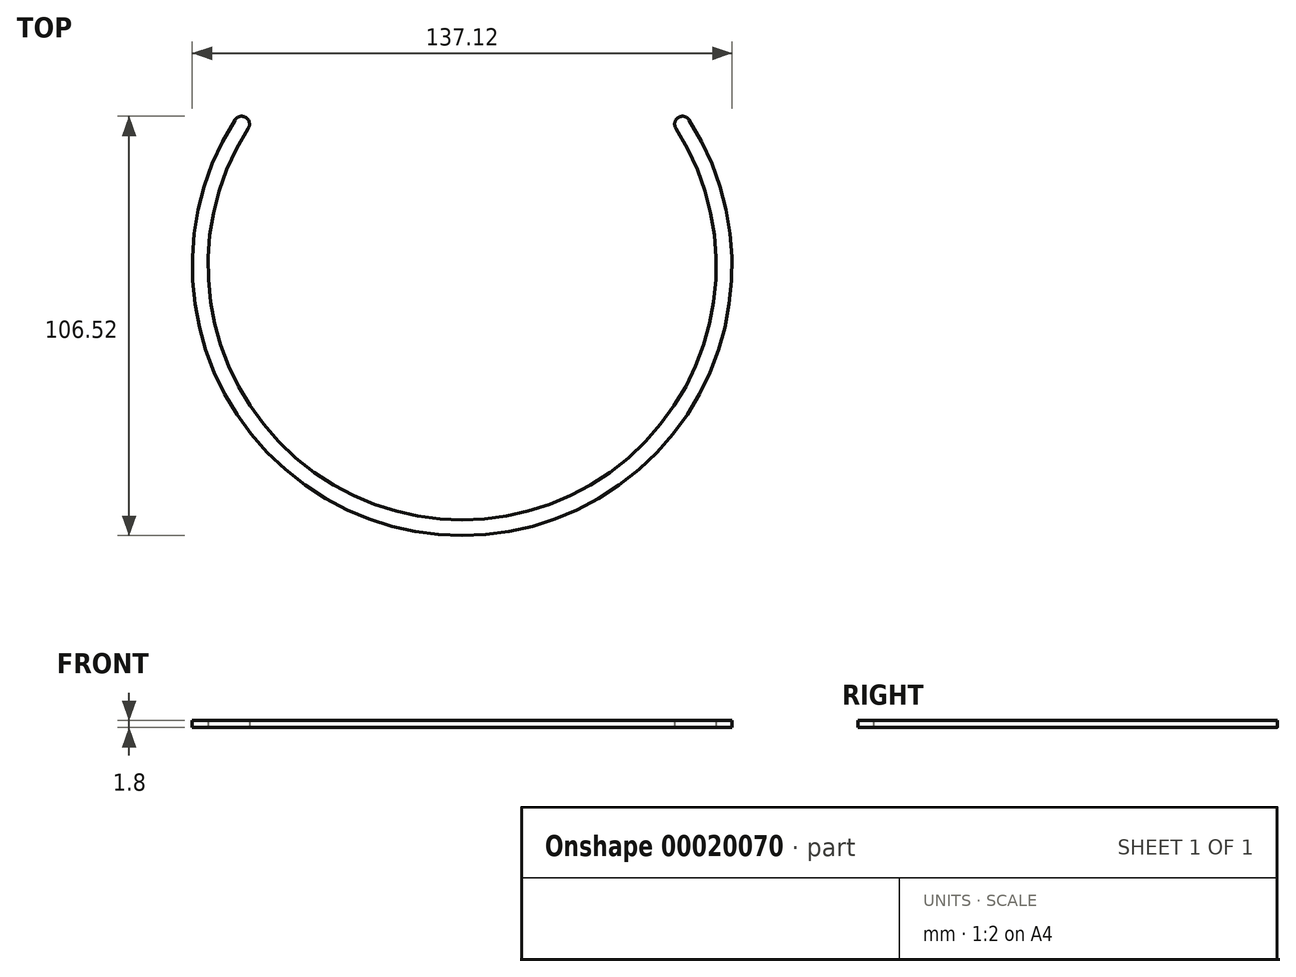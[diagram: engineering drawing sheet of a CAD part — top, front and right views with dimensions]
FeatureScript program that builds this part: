
annotation { "Feature Type Name" : "Feature", "Feature Type Description" : "" }
export const myFeature = defineFeature(function(context is Context, id is Id, definition is map)
    precondition{}
    {
        {
            var Q0;
            Q0=qCreatedBy(makeId("Top.planeOp"),FACE);
            var sketch = newSketch(context, id + "F0", { "sketchPlane" : qUnion([Q0])});
            skArc(sketch, "E0", {"start": v(-53.25, 36.5) * mm, "mid": v(0, -64.56) * mm, "end": v(53.25, 36.5) * mm});
            skArc(sketch, "E1", {"start": v(-56.55, 38.76) * mm, "mid": v(0, -68.56) * mm, "end": v(56.55, 38.76) * mm});
            skLineSegment(sketch, "E2", {"start": v(-53.25, 36.5) * mm, "end": v(-56.55, 38.76) * mm});
            skLineSegment(sketch, "E3", {"start": v(56.55, 38.76) * mm, "end": v(53.25, 36.5) * mm});
            skLineSegment(sketch, "E4", {"start": v(-53.25, 36.5) * mm, "end": v(-53.25, 0) * mm, "construction": true});
            skLineSegment(sketch, "E5", {"start": v(53.25, 36.5) * mm, "end": v(53.25, 0) * mm, "construction": true});
            skSolve(sketch);
        }
        {
            var Q0;
            Q0=makeQuery(id+"F0.imprint","IMPRINT",FACE,{"disambiguationData":[TD([[makeQuery(id+"F0.imprint","IMPRINT",EDGE,{"derivedFrom":sQuery(id+"F0.wireOp",EDGE,"E0")}),-1.0]])]});
            extrude(context, id + "F1", {"entities" : qUnion([Q0]), "depth" : 1.8 * mm});
        }
        {
            var Q0;
            Q0=makeQuery(id+"F1.opExtrude","SWEPT_EDGE",EDGE,{"disambiguationData":[OSD([sQuery(id+"F0.wireOp",EDGE,"E1"),sQuery(id+"F0.wireOp",EDGE,"E2")])]});
            var Q1;
            Q1=makeQuery(id+"F1.opExtrude","SWEPT_EDGE",EDGE,{"disambiguationData":[OSD([sQuery(id+"F0.wireOp",EDGE,"E0"),sQuery(id+"F0.wireOp",EDGE,"E2")])]});
            var Q2;
            Q2=makeQuery(id+"F1.opExtrude","SWEPT_EDGE",EDGE,{"disambiguationData":[OSD([sQuery(id+"F0.wireOp",EDGE,"E0"),sQuery(id+"F0.wireOp",EDGE,"E3")])]});
            var Q3;
            Q3=makeQuery(id+"F1.opExtrude","SWEPT_EDGE",EDGE,{"disambiguationData":[OSD([sQuery(id+"F0.wireOp",EDGE,"E1"),sQuery(id+"F0.wireOp",EDGE,"E3")])]});
            fillet(context, id + "F2", {"entities" : qUnion([Q0, Q1, Q2, Q3]), "radius" : 2 * mm, "tangentPropagation" : true, "allowEdgeOverflow" : false});
        }
    });
